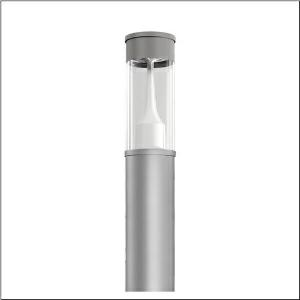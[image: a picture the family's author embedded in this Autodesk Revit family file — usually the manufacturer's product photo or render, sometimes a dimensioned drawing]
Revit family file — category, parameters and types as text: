
# Revit family: city-light_400_iq___p1_0a_5xa5305lf14hp_1a81
name_source: partatom
category: Lighting Fixtures
units: mm (PartAtom-declared; Revit-internal decimal feet)

## family parameters
Cut with Voids When Loaded = No
Host = Face
Light Source = No
Part Type = Normal
Room Calculation Point = No
Round Connector Dimension = Use Diameter
Shared = No

## types (1)
- --- (1 x LED, 4910 lm, 33.6 W, 4000K)
    Apparent Load = 34 VA
    CIE Flux Codes = 31 62 91 95 100
    Color Rendering = 70
    Color Temperature = 4000K
    Default Elevation = 1800 mm
    Description = City-Light 400 iQ, light pillar, Module 540 iQ-SR, primary light control with 3 zone facetted reflector, of plastic, silver coated, highly specular, structured, primary optical cover: cover, of PMMA, transparent, partly coated, light distribution: P1.0a, primary light characteristic: strongly asymmetric, LED, High Power LED, rated luminous flux: 4.910lm, luminous efficacy: 146lm/W, light colour: 740, colour temperature: 4000K, control gear: ECG iQ, control: presetting dimming logarithmic, Street-Remote, Auto-Match, Temp-Guard, Lumen-Switch, Night-Set, Smart-Wire, Light-Fading, Desk-Remote (wireless, voltage-free reading and setting of iQ features in the workshop via application-optimized NFC function/RFID function), optimised constant luminous flux control (CLO 2.0), with terminal, 6-pole, max. 2.5mm², mains connection: 230..240V, AC, 50/60Hz, start of lifetime: 34W, end of service life: 36W, reduction: 15W, luminaire housing, cylindrical, of extruded aluminium section, coated, Siteco® metallic grey (DB 702S), length: 4.694mm, diameter: 200mm, Module 540 iQ-SR, traffic white (RAL 9016), equipment: Power, protection rating (complete): IP65, insulation class (complete): insulation class II (safety insulation), certification: CE, ENEC, VDE, packaging unit: 1 piece

Light Distribution: P1.0a
    Height = 500 mm
    Lamp = 1 x LED
    Lamp Light Flux = 4910 lm
    Lamp Power = 33.6 W
    Lamp count = 1
    Length = 200 mm  [stored 0.656168 ft]
    Luminous efficacy = 146 lm/W
    Manufacturer = Siteco
    ModVariant = No
    Model = 5XA5305LF14HP
    Mounting Place = Floor
    Mounting Type = Freestanding
    Number of Poles = 1
    OnlyDefault = Yes
    Power Factor = 1
    Product Name = City-Light 400 iQ | P1.0a
    Product group = light pillar
    ProductGroupID = 1303
    Protection Class = Protection class II
    Protection Degree = IP 65
    RLX_Detail_Level = 1
    RLX_Emergency_Light_Flux = 0 lm
    RLX_Emergency_Type = 0
    RLX_Emergency_Type_DB = No
    RlxData = <blob elided: 53185 chars, md5=4b226094>
    Socket = socket
    Standby Power = 0 W
    System Light Flux = 4910 lm
    System Power = 34 W
    Type Comments = factory setting: luminous flux: 100 % | dim-lin: 254 | 695 mA
    Type Image = l_1006916.jpg
    URL = http://relux.com
    VarID = @adj_127145
    Voltage = 0 V
    Weight = 0.00 kg
    Width = 0 mm  [stored 0 ft]

note: [stored X ft] marks values corroborated as IEEE doubles in the binary element streams (Revit-internal decimal feet)

## geometry (parser evidence)
native form markers: Blend x4, Sweep x9
no freeform markers — native parametric forms only
